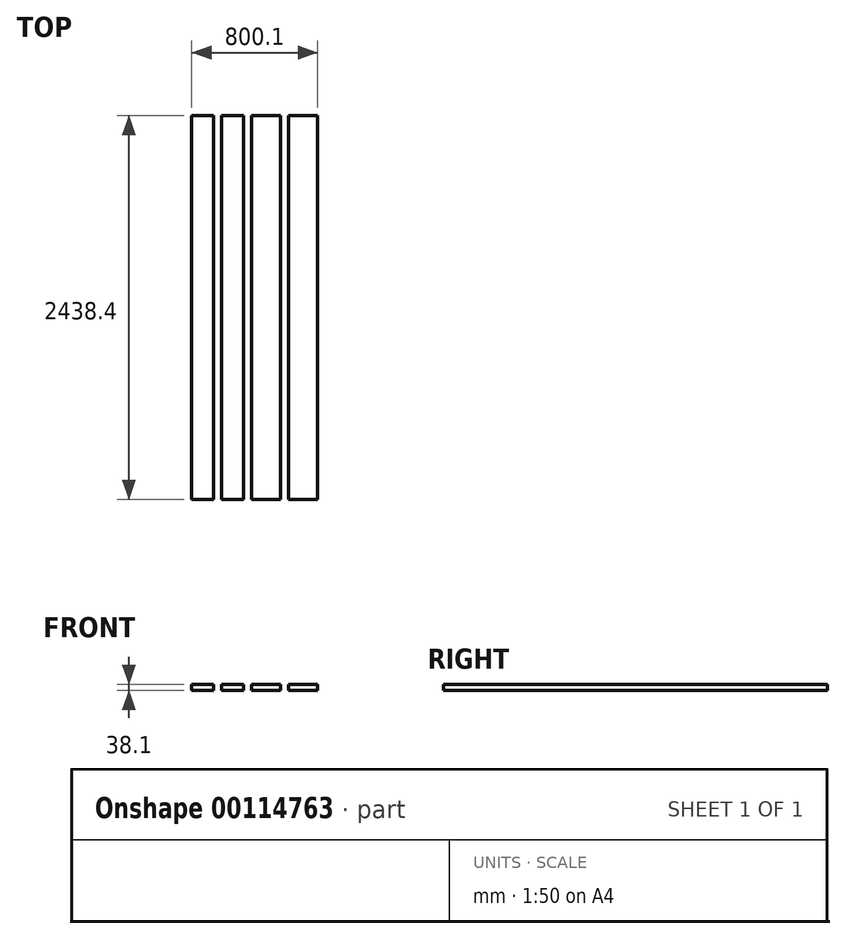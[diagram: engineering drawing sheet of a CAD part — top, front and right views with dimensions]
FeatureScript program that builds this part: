
annotation { "Feature Type Name" : "Feature", "Feature Type Description" : "" }
export const myFeature = defineFeature(function(context is Context, id is Id, definition is map)
    precondition{}
    {
        {
            var Q0;
            Q0=qCreatedBy(makeId("Top.planeOp"),FACE);
            var sketch = newSketch(context, id + "F0", { "sketchPlane" : qUnion([Q0])});
            skLineSegment(sketch, "E0.bottom", {"start": v(0, 0) * mm, "end": v(139.7, 0) * mm});
            skLineSegment(sketch, "E0.top", {"start": v(0, 2438.4) * mm, "end": v(139.7, 2438.4) * mm});
            skLineSegment(sketch, "E0.left", {"start": v(0, 0) * mm, "end": v(0, 2438.4) * mm});
            skLineSegment(sketch, "E0.right", {"start": v(139.7, 0) * mm, "end": v(139.7, 2438.4) * mm});
            skLineSegment(sketch, "E1.bottom", {"start": v(190.5, 0) * mm, "end": v(330.2, 0) * mm});
            skLineSegment(sketch, "E1.top", {"start": v(190.5, 2438.4) * mm, "end": v(330.2, 2438.4) * mm});
            skLineSegment(sketch, "E1.left", {"start": v(190.5, 0) * mm, "end": v(190.5, 2438.4) * mm});
            skLineSegment(sketch, "E1.right", {"start": v(330.2, 0) * mm, "end": v(330.2, 2438.4) * mm});
            skLineSegment(sketch, "E2.bottom", {"start": v(381, 0) * mm, "end": v(565.15, 0) * mm});
            skLineSegment(sketch, "E2.top", {"start": v(381, 2438.4) * mm, "end": v(565.15, 2438.4) * mm});
            skLineSegment(sketch, "E2.left", {"start": v(381, 0) * mm, "end": v(381, 2438.4) * mm});
            skLineSegment(sketch, "E2.right", {"start": v(565.15, 0) * mm, "end": v(565.15, 2438.4) * mm});
            skLineSegment(sketch, "E3.bottom", {"start": v(615.95, 0) * mm, "end": v(800.1, 0) * mm});
            skLineSegment(sketch, "E3.top", {"start": v(615.95, 2438.4) * mm, "end": v(800.1, 2438.4) * mm});
            skLineSegment(sketch, "E3.left", {"start": v(615.95, 0) * mm, "end": v(615.95, 2438.4) * mm});
            skLineSegment(sketch, "E3.right", {"start": v(800.1, 0) * mm, "end": v(800.1, 2438.4) * mm});
            skSolve(sketch);
        }
        {
            var Q0;
            Q0=makeQuery(id+"F0.imprint","IMPRINT",FACE,{"disambiguationData":[TD([[makeQuery(id+"F0.imprint","IMPRINT",EDGE,{"derivedFrom":sQuery(id+"F0.wireOp",EDGE,"E0.bottom")}),1.0]])]});
            var Q1;
            Q1=makeQuery(id+"F0.imprint","IMPRINT",FACE,{"disambiguationData":[TD([[makeQuery(id+"F0.imprint","IMPRINT",EDGE,{"derivedFrom":sQuery(id+"F0.wireOp",EDGE,"E1.bottom")}),1.0]])]});
            var Q2;
            Q2=makeQuery(id+"F0.imprint","IMPRINT",FACE,{"disambiguationData":[TD([[makeQuery(id+"F0.imprint","IMPRINT",EDGE,{"derivedFrom":sQuery(id+"F0.wireOp",EDGE,"E2.bottom")}),1.0]])]});
            var Q3;
            Q3=makeQuery(id+"F0.imprint","IMPRINT",FACE,{"disambiguationData":[TD([[makeQuery(id+"F0.imprint","IMPRINT",EDGE,{"derivedFrom":sQuery(id+"F0.wireOp",EDGE,"E3.bottom")}),1.0]])]});
            extrude(context, id + "F1", {"entities" : qUnion([Q0, Q1, Q2, Q3]), "depth" : 38.1 * mm});
        }
    });
